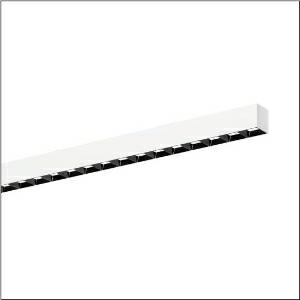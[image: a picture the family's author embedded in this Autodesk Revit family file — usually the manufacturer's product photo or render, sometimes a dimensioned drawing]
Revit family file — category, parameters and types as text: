
# Revit family: silica_r__21_51mx22dc3awb_a852
name_source: partatom
category: Lighting Fixtures
units: mm (PartAtom-declared; Revit-internal decimal feet)

## family parameters
Cut with Voids When Loaded = No
Host = Face
Light Source = No
Part Type = Normal
Room Calculation Point = No
Round Connector Dimension = Use Diameter
Shared = No

## types (1)
- --- (1 x LED, 10800 lm, 69.2 W, 3000K)
    Apparent Load = 69 VA
    CIE Flux Codes = 86 100 100 100 100
    Color Rendering = 80
    Color Temperature = 3000K
    Default Elevation = 1800 mm
    Description = Silica® 21, office luminaire, primary light control with darklight reflector, of PMMA, black, CAT 2 (L<= 3000cd/m²), light emission: direct distribution, primary light characteristic: symmetric, installation type: surface-mounted, LED, rated luminous flux: 10.800lm, luminous efficacy: 156lm/W, light colour: 830, colour temperature: 3000K, control gear: DALI 2, with terminal, 3+2-pole, max. 2.5mm², mains connection: 220..240V, AC, 50/60Hz, rated input power: 69.2W, luminaire housing, of aluminium, traffic white (RAL 9016), length: 3.004mm, width: 53mm, height: 53mm, protection rating (complete): IP20, insulation class (complete): insulation class I (protective earthing), certification: CE, permissible operating ambient temperature: 0..+35°C, standard: EN 50419, packaging unit: 1 piece
    Height = 53 mm
    Lamp = 1 x LED
    Lamp Light Flux = 10800 lm
    Lamp Power = 69.2 W
    Lamp count = 1
    Length = 3004 mm
    Luminous efficacy = 156 lm/W
    Manufacturer = Siteco
    ModVariant = No
    Model = 51MX22DC3AWB
    Mounting Place = Ceiling
    Mounting Type = Surface mounted
    Number of Poles = 1
    OnlyDefault = Yes
    Power Factor = 1
    Product Name = Silica® 21
    Product group = office luminaire | ceiling mounted
    ProductGroupID = 302
    Protection Class = Protection class I
    Protection Degree = IP 20
    RLX_Detail_Level = 1
    RLX_Emergency_Light_Flux = 0 lm
    RLX_Emergency_Type = 0
    RLX_Emergency_Type_DB = No
    RlxData = <blob elided: 61949 chars, md5=4135547e>
    Socket = socket
    Standby Power = 0 W
    System Light Flux = 10800 lm
    System Power = 69 W
    Type Comments = factory setting: luminous flux: 100 % | dim-lin: 254 | 392 mA
    Type Image = l_1335873.jpg
    URL = http://relux.com
    VarID = @adj_124840
    Voltage = 0 V
    Weight = 0.00 kg
    Width = 53 mm

## geometry (parser evidence)
native form markers: Blend x4, Sweep x10
no freeform markers — native parametric forms only
